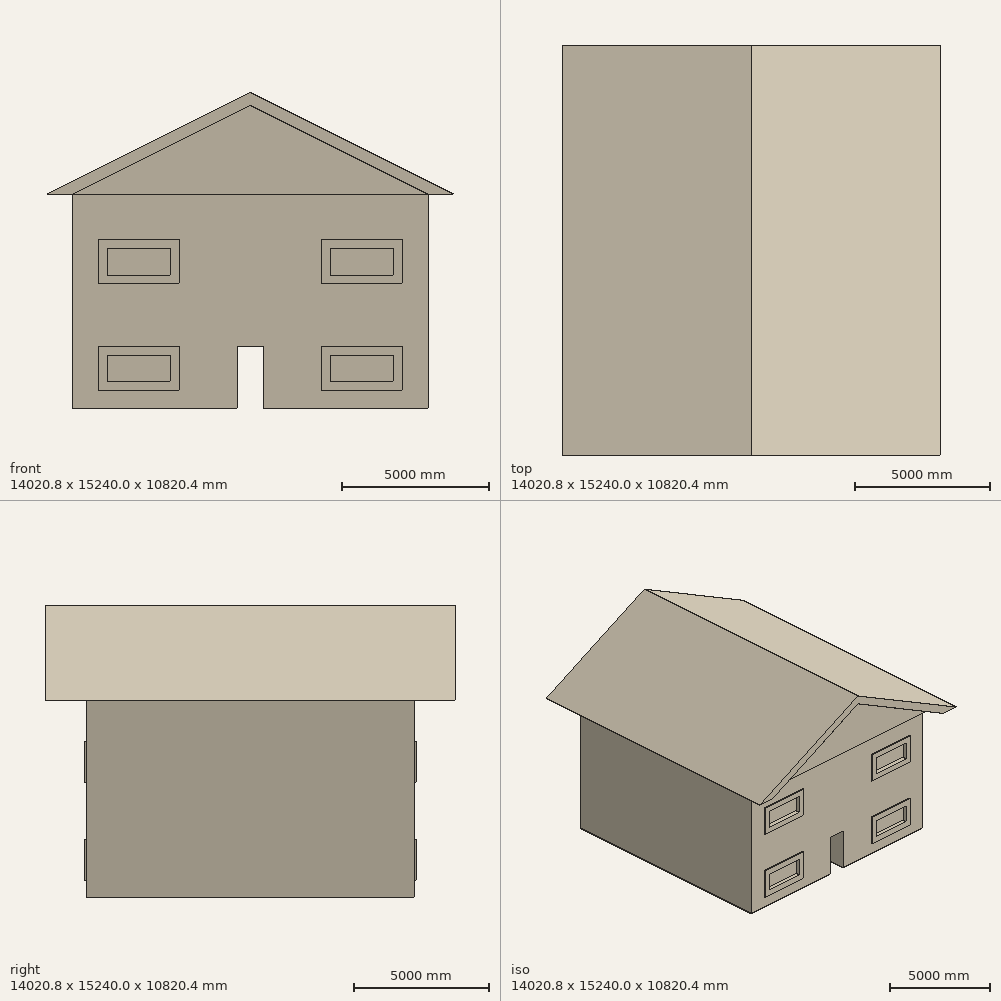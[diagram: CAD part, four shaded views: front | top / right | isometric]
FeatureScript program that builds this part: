
annotation { "Feature Type Name" : "Feature", "Feature Type Description" : "" }
export const myFeature = defineFeature(function(context is Context, id is Id, definition is map)
    precondition{}
    {
        {
            var Q0;
            Q0=qCreatedBy(makeId("Front.planeOp"),FACE);
            var sketch = newSketch(context, id + "F0", { "sketchPlane" : qUnion([Q0])});
            skLineSegment(sketch, "E0", {"start": v(0, 0) * mm, "end": v(-6096, 0) * mm});
            skLineSegment(sketch, "E1", {"start": v(0, 0) * mm, "end": v(6096, 0) * mm});
            skLineSegment(sketch, "E2", {"start": v(0, 0) * mm, "end": v(0, 3048) * mm, "construction": true});
            skLineSegment(sketch, "E3", {"start": v(-6096, 0) * mm, "end": v(0, 3048) * mm});
            skLineSegment(sketch, "E4", {"start": v(0, 3048) * mm, "end": v(6096, 0) * mm});
            skLineSegment(sketch, "E5", {"start": v(-6096, 0) * mm, "end": v(-7010.4, 0) * mm});
            skLineSegment(sketch, "E6", {"start": v(0, 3048) * mm, "end": v(0, 3505.2) * mm});
            skLineSegment(sketch, "E7", {"start": v(-7010.4, 0) * mm, "end": v(0, 3505.2) * mm});
            skLineSegment(sketch, "E8", {"start": v(6096, 0) * mm, "end": v(7010.4, 0) * mm});
            skLineSegment(sketch, "E9", {"start": v(0, 3505.2) * mm, "end": v(7010.4, 0) * mm});
            skLineSegment(sketch, "E10", {"start": v(-6096, 0) * mm, "end": v(-6096, -7315.2) * mm});
            skLineSegment(sketch, "E11", {"start": v(-6096, -7315.2) * mm, "end": v(6096, -7315.2) * mm});
            skLineSegment(sketch, "E12", {"start": v(6096, -7315.2) * mm, "end": v(6096, 0) * mm});
            skLineSegment(sketch, "E13", {"start": v(0, 0) * mm, "end": v(0, -7315.2) * mm, "construction": true});
            skLineSegment(sketch, "E14", {"start": v(0, -7315.2) * mm, "end": v(-457.2, -7315.2) * mm});
            skLineSegment(sketch, "E15", {"start": v(-457.2, -7315.2) * mm, "end": v(0, -7315.2) * mm});
            skLineSegment(sketch, "E16", {"start": v(0, -7315.2) * mm, "end": v(457.2, -7315.2) * mm});
            skLineSegment(sketch, "E17", {"start": v(-457.2, -7315.2) * mm, "end": v(-457.2, -5181.6) * mm});
            skLineSegment(sketch, "E18", {"start": v(457.2, -7315.2) * mm, "end": v(457.2, -5181.6) * mm});
            skLineSegment(sketch, "E19", {"start": v(-457.2, -5181.6) * mm, "end": v(457.2, -5181.6) * mm});
            skLineSegment(sketch, "E20", {"start": v(-6096, -3657.6) * mm, "end": v(6096, -3657.6) * mm});
            skPoint(sketch, "E20.endSnap0", {"position": v(0, -3657.6) * mm});
            skLineSegment(sketch, "E21.bottom", {"start": v(2743.2, -5486.4) * mm, "end": v(4876.8, -5486.4) * mm});
            skLineSegment(sketch, "E21.top", {"start": v(2743.2, -6400.8) * mm, "end": v(4876.8, -6400.8) * mm});
            skLineSegment(sketch, "E21.left", {"start": v(2743.2, -5486.4) * mm, "end": v(2743.2, -6400.8) * mm});
            skLineSegment(sketch, "E21.right", {"start": v(4876.8, -5486.4) * mm, "end": v(4876.8, -6400.8) * mm});
            skLineSegment(sketch, "E22.0", {"start": v(2438.4, -5181.6) * mm, "end": v(5181.6, -5181.6) * mm});
            skLineSegment(sketch, "E22.1", {"start": v(2438.4, -5181.6) * mm, "end": v(2438.4, -6705.6) * mm});
            skLineSegment(sketch, "E22.2", {"start": v(2438.4, -6705.6) * mm, "end": v(5181.6, -6705.6) * mm});
            skLineSegment(sketch, "E22.3", {"start": v(5181.6, -5181.6) * mm, "end": v(5181.6, -6705.6) * mm});
            skLineSegment(sketch, "E23.bottom", {"start": v(-4876.8, -1828.8) * mm, "end": v(-2743.2, -1828.8) * mm});
            skLineSegment(sketch, "E23.top", {"start": v(-4876.8, -2743.2) * mm, "end": v(-2743.2, -2743.2) * mm});
            skLineSegment(sketch, "E23.left", {"start": v(-4876.8, -1828.8) * mm, "end": v(-4876.8, -2743.2) * mm});
            skLineSegment(sketch, "E23.right", {"start": v(-2743.2, -1828.8) * mm, "end": v(-2743.2, -2743.2) * mm});
            skLineSegment(sketch, "E24.0", {"start": v(-5181.6, -1524) * mm, "end": v(-2438.4, -1524) * mm});
            skLineSegment(sketch, "E24.1", {"start": v(-5181.6, -1524) * mm, "end": v(-5181.6, -3048) * mm});
            skLineSegment(sketch, "E24.2", {"start": v(-5181.6, -3048) * mm, "end": v(-2438.4, -3048) * mm});
            skLineSegment(sketch, "E24.3", {"start": v(-2438.4, -1524) * mm, "end": v(-2438.4, -3048) * mm});
            skLineSegment(sketch, "E25.bottom", {"start": v(2743.2, -1828.8) * mm, "end": v(4876.8, -1828.8) * mm});
            skLineSegment(sketch, "E25.top", {"start": v(2743.2, -2743.2) * mm, "end": v(4876.8, -2743.2) * mm});
            skLineSegment(sketch, "E25.left", {"start": v(2743.2, -1828.8) * mm, "end": v(2743.2, -2743.2) * mm});
            skLineSegment(sketch, "E25.right", {"start": v(4876.8, -1828.8) * mm, "end": v(4876.8, -2743.2) * mm});
            skLineSegment(sketch, "E26.0", {"start": v(2438.4, -1524) * mm, "end": v(5181.6, -1524) * mm});
            skLineSegment(sketch, "E26.1", {"start": v(2438.4, -1524) * mm, "end": v(2438.4, -3048) * mm});
            skLineSegment(sketch, "E26.2", {"start": v(2438.4, -3048) * mm, "end": v(5181.6, -3048) * mm});
            skLineSegment(sketch, "E26.3", {"start": v(5181.6, -1524) * mm, "end": v(5181.6, -3048) * mm});
            skLineSegment(sketch, "E27.bottom", {"start": v(-4876.8, -5486.4) * mm, "end": v(-2743.2, -5486.4) * mm});
            skLineSegment(sketch, "E27.top", {"start": v(-4876.8, -6400.8) * mm, "end": v(-2743.2, -6400.8) * mm});
            skLineSegment(sketch, "E27.left", {"start": v(-4876.8, -5486.4) * mm, "end": v(-4876.8, -6400.8) * mm});
            skLineSegment(sketch, "E27.right", {"start": v(-2743.2, -5486.4) * mm, "end": v(-2743.2, -6400.8) * mm});
            skLineSegment(sketch, "E28.0", {"start": v(-5181.6, -5181.6) * mm, "end": v(-2438.4, -5181.6) * mm});
            skLineSegment(sketch, "E28.1", {"start": v(-5181.6, -5181.6) * mm, "end": v(-5181.6, -6705.6) * mm});
            skLineSegment(sketch, "E28.2", {"start": v(-5181.6, -6705.6) * mm, "end": v(-2438.4, -6705.6) * mm});
            skLineSegment(sketch, "E28.3", {"start": v(-2438.4, -5181.6) * mm, "end": v(-2438.4, -6705.6) * mm});
            skSolve(sketch);
        }
        {
            var Q0;
            {var subQ0=sQuery(id+"F0.wireOp",EDGE,"E0");Q0=makeQuery(id+"F0.imprint","IMPRINT",FACE,{"disambiguationData":[TD([[makeQuery(id+"F0.imprint","IMPRINT",EDGE,{"derivedFrom":subQ0}),1.0]])]});}
            var Q1;
            {var subQ2=sQuery(id+"F0.wireOp",EDGE,"E17");Q1=makeQuery(id+"F0.imprint","IMPRINT",FACE,{"disambiguationData":[TD([[makeQuery(id+"F0.imprint","IMPRINT",EDGE,{"derivedFrom":subQ2}),1.0]])]});}
            extrude(context, id + "F1", {"entities" : qUnion([Q0, Q1]), "endBound" : BoundingType.SYMMETRIC, "depth" : 12192 * mm, "offsetDistance" : 30.48 * mm});
        }
        {
            var Q0;
            Q0=makeQuery(id+"F0.imprint","IMPRINT",FACE,{"disambiguationData":[TD([[makeQuery(id+"F0.imprint","IMPRINT",EDGE,{"derivedFrom":sQuery(id+"F0.wireOp",EDGE,"E23.bottom")}),-1.0]])]});
            var Q1;
            Q1=makeQuery(id+"F0.imprint","IMPRINT",FACE,{"disambiguationData":[TD([[makeQuery(id+"F0.imprint","IMPRINT",EDGE,{"derivedFrom":sQuery(id+"F0.wireOp",EDGE,"E27.bottom")}),-1.0]])]});
            var Q2;
            Q2=makeQuery(id+"F0.imprint","IMPRINT",FACE,{"disambiguationData":[TD([[makeQuery(id+"F0.imprint","IMPRINT",EDGE,{"derivedFrom":sQuery(id+"F0.wireOp",EDGE,"E21.bottom")}),-1.0]])]});
            var Q3;
            Q3=makeQuery(id+"F0.imprint","IMPRINT",FACE,{"disambiguationData":[TD([[makeQuery(id+"F0.imprint","IMPRINT",EDGE,{"derivedFrom":sQuery(id+"F0.wireOp",EDGE,"E25.bottom")}),-1.0]])]});
            extrude(context, id + "F2", {"entities" : qUnion([Q0, Q1, Q2, Q3]), "endBound" : BoundingType.SYMMETRIC, "depth" : 11887.2 * mm, "offsetDistance" : 30.48 * mm});
        }
        {
            var Q0;
            Q0=makeQuery(id+"F0.imprint","IMPRINT",FACE,{"disambiguationData":[TD([[makeQuery(id+"F0.imprint","IMPRINT",EDGE,{"derivedFrom":sQuery(id+"F0.wireOp",EDGE,"E15")}),1.0]])]});
            var Q1;
            Q1=makeQuery(id+"F0.imprint","IMPRINT",FACE,{"disambiguationData":[TD([[makeQuery(id+"F0.imprint","IMPRINT",EDGE,{"derivedFrom":sQuery(id+"F0.wireOp",EDGE,"E21.bottom")}),1.0]])]});
            var Q2;
            Q2=makeQuery(id+"F0.imprint","IMPRINT",FACE,{"disambiguationData":[TD([[makeQuery(id+"F0.imprint","IMPRINT",EDGE,{"derivedFrom":sQuery(id+"F0.wireOp",EDGE,"E25.bottom")}),1.0]])]});
            var Q3;
            Q3=makeQuery(id+"F0.imprint","IMPRINT",FACE,{"disambiguationData":[TD([[makeQuery(id+"F0.imprint","IMPRINT",EDGE,{"derivedFrom":sQuery(id+"F0.wireOp",EDGE,"E23.bottom")}),1.0]])]});
            var Q4;
            Q4=makeQuery(id+"F0.imprint","IMPRINT",FACE,{"disambiguationData":[TD([[makeQuery(id+"F0.imprint","IMPRINT",EDGE,{"derivedFrom":sQuery(id+"F0.wireOp",EDGE,"E27.bottom")}),1.0]])]});
            extrude(context, id + "F3", {"entities" : qUnion([Q0, Q1, Q2, Q3, Q4]), "endBound" : BoundingType.SYMMETRIC, "depth" : 12344.4 * mm, "offsetDistance" : 30.48 * mm});
        }
        {
            var Q0;
            Q0=makeQuery(id+"F0.imprint","IMPRINT",FACE,{"disambiguationData":[TD([[makeQuery(id+"F0.imprint","IMPRINT",EDGE,{"derivedFrom":sQuery(id+"F0.wireOp",EDGE,"E4")}),1.0]])]});
            var Q1;
            Q1=makeQuery(id+"F0.imprint","IMPRINT",FACE,{"disambiguationData":[TD([[makeQuery(id+"F0.imprint","IMPRINT",EDGE,{"derivedFrom":sQuery(id+"F0.wireOp",EDGE,"E3")}),1.0]])]});
            extrude(context, id + "F4", {"entities" : qUnion([Q0, Q1]), "endBound" : BoundingType.SYMMETRIC, "depth" : 15240 * mm, "offsetDistance" : 30.48 * mm});
        }
        {
            var Q0;
            Q0=makeQuery(id+"F0.imprint","IMPRINT",FACE,{"disambiguationData":[TD([[makeQuery(id+"F0.imprint","IMPRINT",EDGE,{"derivedFrom":sQuery(id+"F0.wireOp",EDGE,"E0")}),-1.0]])]});
            extrude(context, id + "F5", {"entities" : qUnion([Q0]), "endBound" : BoundingType.SYMMETRIC, "depth" : 13716 * mm, "offsetDistance" : 30.48 * mm});
        }
    });
